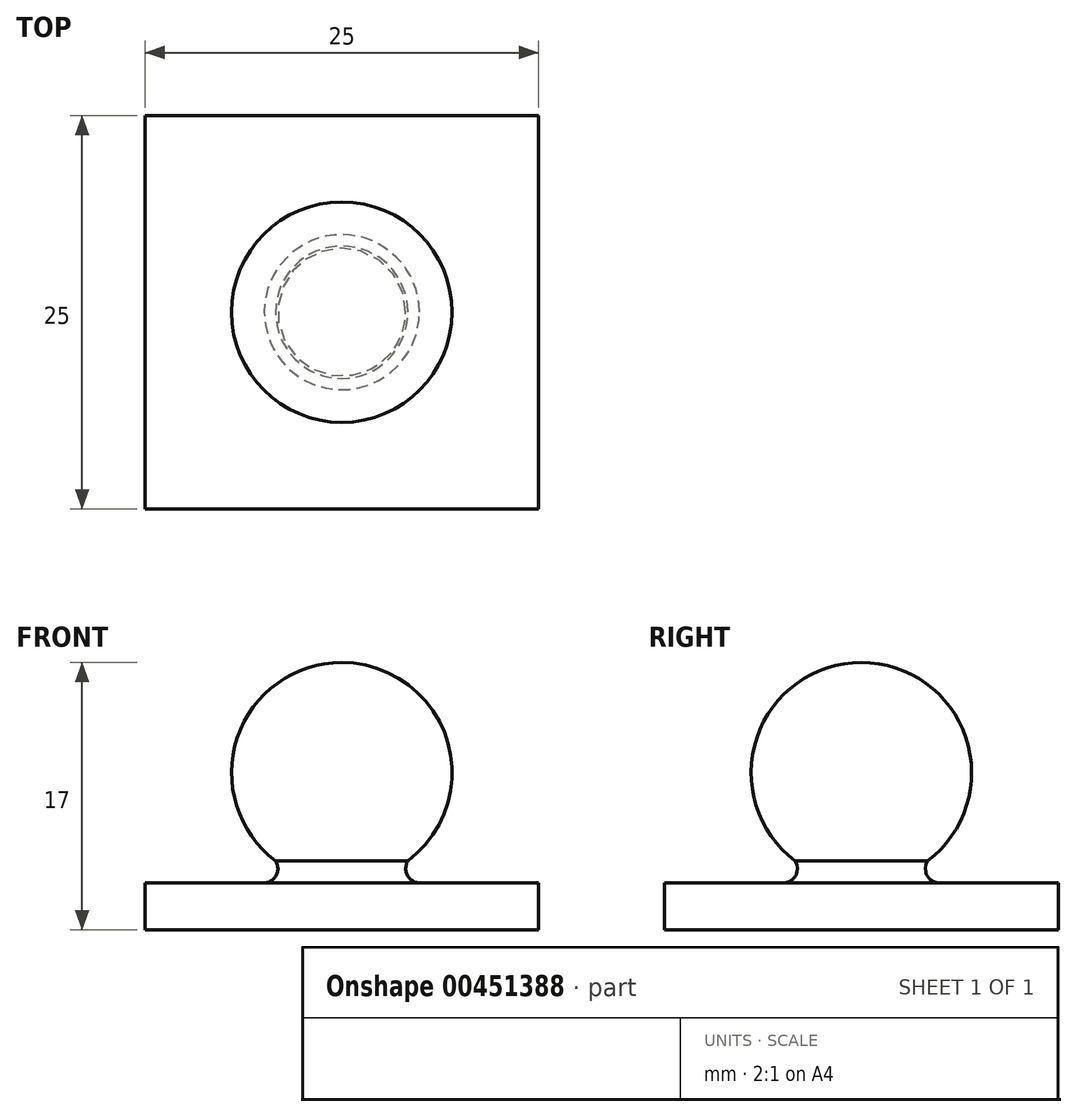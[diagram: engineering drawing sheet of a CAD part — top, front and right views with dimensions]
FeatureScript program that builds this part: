
annotation { "Feature Type Name" : "Feature", "Feature Type Description" : "" }
export const myFeature = defineFeature(function(context is Context, id is Id, definition is map)
    precondition{}
    {
        {
            var Q0;
            Q0=qCreatedBy(makeId("Top.planeOp"),FACE);
            var sketch = newSketch(context, id + "F0", { "sketchPlane" : qUnion([Q0])});
            skLineSegment(sketch, "E0.bottom", {"start": v(-12.5, -12.5) * mm, "end": v(12.5, -12.5) * mm});
            skLineSegment(sketch, "E0.top", {"start": v(-12.5, 12.5) * mm, "end": v(12.5, 12.5) * mm});
            skLineSegment(sketch, "E0.left", {"start": v(-12.5, -12.5) * mm, "end": v(-12.5, 12.5) * mm});
            skLineSegment(sketch, "E0.right", {"start": v(12.5, -12.5) * mm, "end": v(12.5, 12.5) * mm});
            skPoint(sketch, "E0.middle", {"position": v(0, 0) * mm});
            skSolve(sketch);
        }
        {
            var Q0;
            Q0=makeQuery(id+"F0.imprint","IMPRINT",FACE,{"disambiguationData":[TD([[makeQuery(id+"F0.imprint","IMPRINT",EDGE,{"derivedFrom":sQuery(id+"F0.wireOp",EDGE,"E0.bottom")}),1.0]])]});
            extrude(context, id + "F1", {"entities" : qUnion([Q0]), "depth" : 3 * mm});
        }
        {
            var Q0;
            Q0=qCreatedBy(makeId("Front.planeOp"),FACE);
            var sketch = newSketch(context, id + "F2", { "sketchPlane" : qUnion([Q0])});
            skLineSegment(sketch, "E1", {"start": v(0, 10) * mm, "end": v(0, 3) * mm});
            skArc(sketch, "E2", {"start": v(0, 3) * mm, "mid": v(7, 10) * mm, "end": v(0, 17) * mm});
            skArc(sketch, "E3", {"start": v(4.2, 4.4) * mm, "mid": v(4.18, 3.45) * mm, "end": v(5.02, 3) * mm});
            skLineSegment(sketch, "E4", {"start": v(5.02, 3) * mm, "end": v(0, 3) * mm});
            skLineSegment(sketch, "E5", {"start": v(0, 17) * mm, "end": v(0, 10) * mm});
            skSolve(sketch);
        }
        {
            var Q0;
            {var subQ0=sQuery(id+"F2.wireOp",EDGE,"E1");Q0=makeQuery(id+"F2.imprint","IMPRINT",FACE,{"disambiguationData":[TD([[makeQuery(id+"F2.imprint","IMPRINT",EDGE,{"derivedFrom":subQ0}),1.0]])]});}
            var Q1;
            {var subQ1=sQuery(id+"F2.wireOp",EDGE,"E2");var subQ3=sQuery(id+"F2.wireOp",EDGE,"E3");var subQ4=makeQuery(id+"F2.imprint","INTERSECT",VERTEX,{"derivedFrom":[subQ1,subQ3]});Q1=makeQuery(id+"F2.imprint","IMPRINT",FACE,{"disambiguationData":[TD([[makeQuery(id+"F2.imprint","IMPRINT",EDGE,{"disambiguationData":[TD([[subQ4,-1.0]])],"derivedFrom":subQ3}),-1.0]])]});}
            var Q2;
            Q2=sQuery(id+"F2.wireOp",EDGE,"E1");
            revolve(context, id + "F3", {"entities" : qUnion([Q0, Q1]), "axis" : qUnion([Q2]), "revolveType" : RevolveType.FULL});
        }
    });
